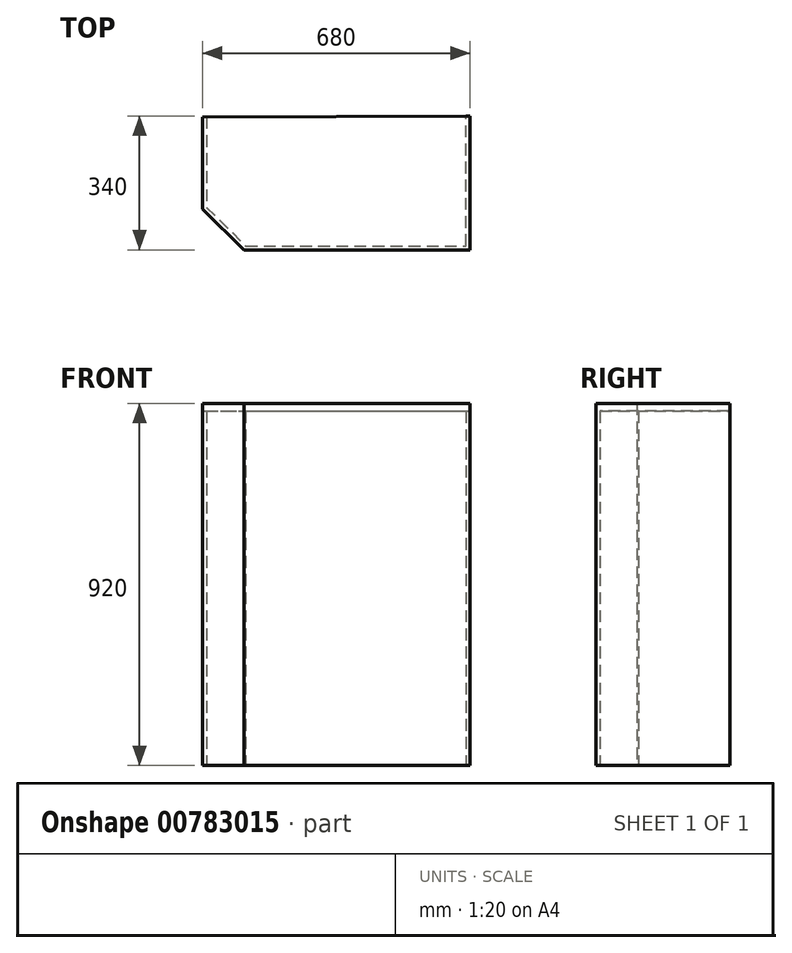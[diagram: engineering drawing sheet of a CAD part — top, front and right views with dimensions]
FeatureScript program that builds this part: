
annotation { "Feature Type Name" : "Feature", "Feature Type Description" : "" }
export const myFeature = defineFeature(function(context is Context, id is Id, definition is map)
    precondition{}
    {
        {
            var Q0;
            Q0=qCreatedBy(makeId("Top.planeOp"),FACE);
            var sketch = newSketch(context, id + "F0", { "sketchPlane" : qUnion([Q0])});
            skLineSegment(sketch, "E0", {"start": v(0, 330) * mm, "end": v(0, 100) * mm});
            skLineSegment(sketch, "E1", {"start": v(100, 2.3) * mm, "end": v(660, 2.3) * mm});
            skLineSegment(sketch, "E2", {"start": v(660, 2.3) * mm, "end": v(660, 332.3) * mm});
            skLineSegment(sketch, "E3", {"start": v(0, 100) * mm, "end": v(100, 2.3) * mm});
            skLineSegment(sketch, "E4.0", {"start": v(670, -7.7) * mm, "end": v(670, 332.3) * mm});
            skLineSegment(sketch, "E4.1", {"start": v(95.93, -7.7) * mm, "end": v(670, -7.7) * mm});
            skLineSegment(sketch, "E4.2", {"start": v(-10, 95.79) * mm, "end": v(95.93, -7.7) * mm});
            skLineSegment(sketch, "E4.3", {"start": v(-10, 330) * mm, "end": v(-10, 95.79) * mm});
            skLineSegment(sketch, "E5", {"start": v(-10, 330) * mm, "end": v(0, 330) * mm});
            skLineSegment(sketch, "E6", {"start": v(660, 332.3) * mm, "end": v(670, 332.3) * mm});
            skSolve(sketch);
        }
        {
            var Q0;
            Q0 = qSketchRegion(id + "F0", true);
            extrude(context, id + "F1", {"entities" : qUnion([Q0]), "depth" : 900 * mm, "offsetDistance" : 25 * mm});
        }
        {
            var Q0;
            Q0=makeQuery(id+"F1.opExtrude","CAP_FACE",FACE,{"disambiguationData":[OSD([sQuery(id+"F0.wireOp",EDGE,"E0"),sQuery(id+"F0.wireOp",EDGE,"E1"),sQuery(id+"F0.wireOp",EDGE,"E2"),sQuery(id+"F0.wireOp",EDGE,"E3"),sQuery(id+"F0.wireOp",EDGE,"E4.0"),sQuery(id+"F0.wireOp",EDGE,"E4.1"),sQuery(id+"F0.wireOp",EDGE,"E4.2"),sQuery(id+"F0.wireOp",EDGE,"E4.3"),sQuery(id+"F0.wireOp",EDGE,"E5"),sQuery(id+"F0.wireOp",EDGE,"E6")])],"isStart":false});
            var sketch = newSketch(context, id + "F2", { "sketchPlane" : qUnion([Q0])});
            skLineSegment(sketch, "E7", {"start": v(-10, 330) * mm, "end": v(670, 332.3) * mm});
            skLineSegment(sketch, "E8", {"start": v(670, 332.3) * mm, "end": v(670, -7.7) * mm});
            skLineSegment(sketch, "E9", {"start": v(670, -7.7) * mm, "end": v(95.93, -7.7) * mm});
            skLineSegment(sketch, "E10", {"start": v(95.93, -7.7) * mm, "end": v(-10, 95.79) * mm});
            skLineSegment(sketch, "E11", {"start": v(-10, 95.79) * mm, "end": v(-10, 330) * mm});
            skSolve(sketch);
        }
        {
            var Q0;
            Q0 = qSketchRegion(id + "F2", true);
            extrude(context, id + "F3", {"entities" : qUnion([Q0]), "operationType" : NewBodyOperationType.ADD, "depth" : 20 * mm, "offsetDistance" : 25 * mm});
        }
    });
